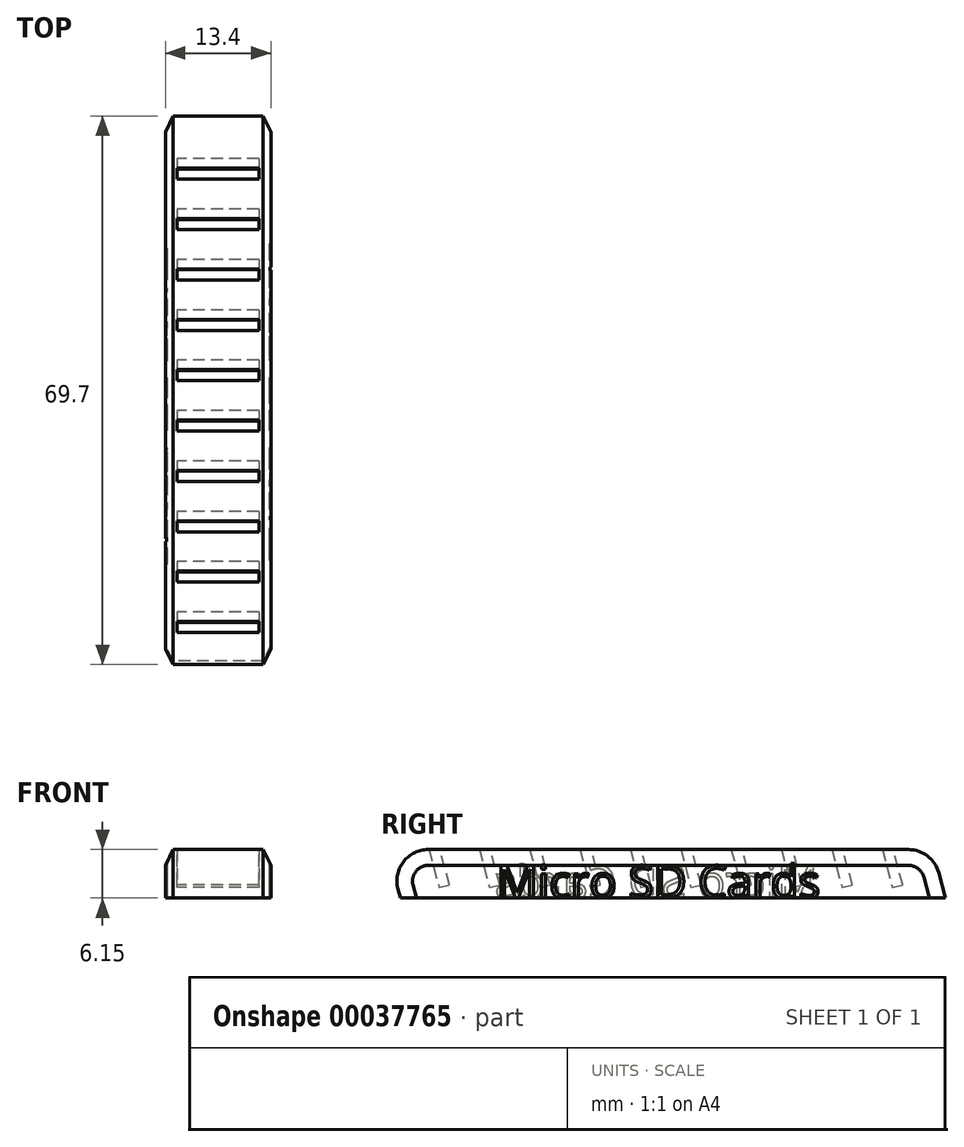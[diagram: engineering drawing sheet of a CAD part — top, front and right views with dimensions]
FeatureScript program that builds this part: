
annotation { "Feature Type Name" : "Feature", "Feature Type Description" : "" }
export const myFeature = defineFeature(function(context is Context, id is Id, definition is map)
    precondition{}
    {
        {
            assignVariable(context, id + "F0", {"name" : "tolerance", "anyValue" : 0.6});
        }
        {
            var Q0;
            Q0=qCreatedBy(makeId("Right.planeOp"),FACE);
            var sketch = newSketch(context, id + "F1", { "sketchPlane" : qUnion([Q0])});
            skLineSegment(sketch, "E0.bottom", {"start": v(-7.62, 0) * mm, "end": v(61.65, 0) * mm});
            skLineSegment(sketch, "E0.top", {"start": v(-9.26, 6.15) * mm, "end": v(60, 6.15) * mm, "construction": true});
            skLineSegment(sketch, "E1", {"start": v(-3.97, 6.15) * mm, "end": v(-2.68, 1.32) * mm});
            skLineSegment(sketch, "E2", {"start": v(-2.68, 1.32) * mm, "end": v(-1.37, 1.67) * mm});
            skLineSegment(sketch, "E3", {"start": v(-1.37, 1.67) * mm, "end": v(-2.57, 6.15) * mm});
            skLineSegment(sketch, "E4", {"start": v(-2.57, 6.15) * mm, "end": v(2.43, 6.15) * mm});
            skLineSegment(sketch, "E5.1.0.0", {"start": v(2.43, 6.15) * mm, "end": v(3.72, 1.32) * mm});
            skLineSegment(sketch, "E5.1.0.1", {"start": v(3.72, 1.32) * mm, "end": v(5.03, 1.67) * mm});
            skLineSegment(sketch, "E5.1.0.2", {"start": v(5.03, 1.67) * mm, "end": v(3.82, 6.15) * mm});
            skLineSegment(sketch, "E5.1.0.3", {"start": v(3.82, 6.15) * mm, "end": v(8.82, 6.15) * mm});
            skLineSegment(sketch, "E5.direction1", {"start": v(-2.68, 1.32) * mm, "end": v(3.72, 1.32) * mm, "construction": true});
            skLineSegment(sketch, "E6", {"start": v(-9.26, 6.15) * mm, "end": v(-3.97, 6.15) * mm});
            skLineSegment(sketch, "E7.0.2.0", {"start": v(8.82, 6.15) * mm, "end": v(10.12, 1.32) * mm});
            skLineSegment(sketch, "E7.3.2.0", {"start": v(10.12, 1.32) * mm, "end": v(11.42, 1.67) * mm});
            skLineSegment(sketch, "E7.6.2.0", {"start": v(11.42, 1.67) * mm, "end": v(10.22, 6.15) * mm});
            skLineSegment(sketch, "E7.9.2.0", {"start": v(10.22, 6.15) * mm, "end": v(15.22, 6.15) * mm});
            skLineSegment(sketch, "E8.0.3.0", {"start": v(15.22, 6.15) * mm, "end": v(16.52, 1.32) * mm});
            skLineSegment(sketch, "E8.3.3.0", {"start": v(16.52, 1.32) * mm, "end": v(17.82, 1.67) * mm});
            skLineSegment(sketch, "E8.6.3.0", {"start": v(17.82, 1.67) * mm, "end": v(16.62, 6.15) * mm});
            skLineSegment(sketch, "E8.9.3.0", {"start": v(16.62, 6.15) * mm, "end": v(21.62, 6.15) * mm});
            skLineSegment(sketch, "E9", {"start": v(60, 6.15) * mm, "end": v(61.65, 0) * mm});
            skLineSegment(sketch, "E10", {"start": v(-9.26, 6.15) * mm, "end": v(-7.62, 0) * mm});
            skLineSegment(sketch, "E11.0.4.0", {"start": v(21.62, 6.15) * mm, "end": v(22.91, 1.32) * mm});
            skLineSegment(sketch, "E11.3.4.0", {"start": v(22.91, 1.32) * mm, "end": v(24.22, 1.67) * mm});
            skLineSegment(sketch, "E11.6.4.0", {"start": v(24.22, 1.67) * mm, "end": v(23.02, 6.15) * mm});
            skLineSegment(sketch, "E11.9.4.0", {"start": v(23.02, 6.15) * mm, "end": v(28.02, 6.15) * mm});
            skLineSegment(sketch, "E11.0.5.0", {"start": v(28.02, 6.15) * mm, "end": v(29.31, 1.32) * mm});
            skLineSegment(sketch, "E11.3.5.0", {"start": v(29.31, 1.32) * mm, "end": v(30.62, 1.67) * mm});
            skLineSegment(sketch, "E11.6.5.0", {"start": v(30.62, 1.67) * mm, "end": v(29.42, 6.15) * mm});
            skLineSegment(sketch, "E11.9.5.0", {"start": v(29.42, 6.15) * mm, "end": v(34.42, 6.15) * mm});
            skLineSegment(sketch, "E11.0.6.0", {"start": v(34.42, 6.15) * mm, "end": v(35.7, 1.32) * mm});
            skLineSegment(sketch, "E11.3.6.0", {"start": v(35.7, 1.32) * mm, "end": v(37.01, 1.67) * mm});
            skLineSegment(sketch, "E11.6.6.0", {"start": v(37.01, 1.67) * mm, "end": v(35.81, 6.15) * mm});
            skLineSegment(sketch, "E11.9.6.0", {"start": v(35.81, 6.15) * mm, "end": v(40.81, 6.15) * mm});
            skLineSegment(sketch, "E11.0.7.0", {"start": v(40.81, 6.15) * mm, "end": v(42.1, 1.32) * mm});
            skLineSegment(sketch, "E11.3.7.0", {"start": v(42.1, 1.32) * mm, "end": v(43.41, 1.67) * mm});
            skLineSegment(sketch, "E11.6.7.0", {"start": v(43.41, 1.67) * mm, "end": v(42.21, 6.15) * mm});
            skLineSegment(sketch, "E11.9.7.0", {"start": v(42.21, 6.15) * mm, "end": v(47.21, 6.15) * mm});
            skLineSegment(sketch, "E11.0.8.0", {"start": v(47.21, 6.15) * mm, "end": v(48.5, 1.32) * mm});
            skLineSegment(sketch, "E11.3.8.0", {"start": v(48.5, 1.32) * mm, "end": v(49.8, 1.67) * mm});
            skLineSegment(sketch, "E11.6.8.0", {"start": v(49.8, 1.67) * mm, "end": v(48.6, 6.15) * mm});
            skLineSegment(sketch, "E11.9.8.0", {"start": v(48.6, 6.15) * mm, "end": v(53.6, 6.15) * mm});
            skLineSegment(sketch, "E11.0.9.0", {"start": v(53.6, 6.15) * mm, "end": v(54.9, 1.32) * mm});
            skLineSegment(sketch, "E11.3.9.0", {"start": v(54.9, 1.32) * mm, "end": v(56.2, 1.67) * mm});
            skLineSegment(sketch, "E11.6.9.0", {"start": v(56.2, 1.67) * mm, "end": v(55, 6.15) * mm});
            skLineSegment(sketch, "E11.9.9.0", {"start": v(55, 6.15) * mm, "end": v(60, 6.15) * mm});
            skSolve(sketch);
        }
        {
            var Q0;
            Q0=makeQuery(id+"F1.imprint","IMPRINT",FACE,{"disambiguationData":[TD([[makeQuery(id+"F1.imprint","IMPRINT",EDGE,{"derivedFrom":sQuery(id+"F1.wireOp",EDGE,"E0.bottom")}),1.0]])]});
            extrude(context, id + "F2", {"entities" : qUnion([Q0]), "depth" : (9.8 + getVariable(context, 'tolerance')) / 2 * mm});
        }
        {
            var Q0;
            Q0=makeQuery(id+"F2.opExtrude","CAP_FACE",FACE,{"disambiguationData":[OSD([sQuery(id+"F1.wireOp",EDGE,"E0.bottom"),sQuery(id+"F1.wireOp",EDGE,"E1"),sQuery(id+"F1.wireOp",EDGE,"E2"),sQuery(id+"F1.wireOp",EDGE,"E3"),sQuery(id+"F1.wireOp",EDGE,"E4"),sQuery(id+"F1.wireOp",EDGE,"E5.1.0.0"),sQuery(id+"F1.wireOp",EDGE,"E5.1.0.1"),sQuery(id+"F1.wireOp",EDGE,"E5.1.0.2"),sQuery(id+"F1.wireOp",EDGE,"E5.1.0.3"),sQuery(id+"F1.wireOp",EDGE,"E6"),sQuery(id+"F1.wireOp",EDGE,"E7.0.2.0"),sQuery(id+"F1.wireOp",EDGE,"E7.3.2.0"),sQuery(id+"F1.wireOp",EDGE,"E7.6.2.0"),sQuery(id+"F1.wireOp",EDGE,"E7.9.2.0"),sQuery(id+"F1.wireOp",EDGE,"E8.0.3.0"),sQuery(id+"F1.wireOp",EDGE,"E8.3.3.0"),sQuery(id+"F1.wireOp",EDGE,"E8.6.3.0"),sQuery(id+"F1.wireOp",EDGE,"E8.9.3.0"),sQuery(id+"F1.wireOp",EDGE,"E9"),sQuery(id+"F1.wireOp",EDGE,"E10"),sQuery(id+"F1.wireOp",EDGE,"E11.0.4.0"),sQuery(id+"F1.wireOp",EDGE,"E11.3.4.0"),sQuery(id+"F1.wireOp",EDGE,"E11.6.4.0"),sQuery(id+"F1.wireOp",EDGE,"E11.9.4.0"),sQuery(id+"F1.wireOp",EDGE,"E11.0.5.0"),sQuery(id+"F1.wireOp",EDGE,"E11.3.5.0"),sQuery(id+"F1.wireOp",EDGE,"E11.6.5.0"),sQuery(id+"F1.wireOp",EDGE,"E11.9.5.0"),sQuery(id+"F1.wireOp",EDGE,"E11.0.6.0"),sQuery(id+"F1.wireOp",EDGE,"E11.3.6.0"),sQuery(id+"F1.wireOp",EDGE,"E11.6.6.0"),sQuery(id+"F1.wireOp",EDGE,"E11.9.6.0"),sQuery(id+"F1.wireOp",EDGE,"E11.0.7.0"),sQuery(id+"F1.wireOp",EDGE,"E11.3.7.0"),sQuery(id+"F1.wireOp",EDGE,"E11.6.7.0"),sQuery(id+"F1.wireOp",EDGE,"E11.9.7.0"),sQuery(id+"F1.wireOp",EDGE,"E11.0.8.0"),sQuery(id+"F1.wireOp",EDGE,"E11.3.8.0"),sQuery(id+"F1.wireOp",EDGE,"E11.6.8.0"),sQuery(id+"F1.wireOp",EDGE,"E11.9.8.0"),sQuery(id+"F1.wireOp",EDGE,"E11.0.9.0"),sQuery(id+"F1.wireOp",EDGE,"E11.3.9.0"),sQuery(id+"F1.wireOp",EDGE,"E11.6.9.0"),sQuery(id+"F1.wireOp",EDGE,"E11.9.9.0")])],"isStart":false});
            var sketch = newSketch(context, id + "F3", { "sketchPlane" : qUnion([Q0])});
            skLineSegment(sketch, "E12", {"start": v(-9.26, 6.15) * mm, "end": v(-7.62, 0) * mm});
            skLineSegment(sketch, "E13", {"start": v(-7.62, 0) * mm, "end": v(61.65, 0) * mm});
            skLineSegment(sketch, "E14", {"start": v(61.65, 0) * mm, "end": v(60, 6.15) * mm});
            skLineSegment(sketch, "E15", {"start": v(60, 6.15) * mm, "end": v(-9.26, 6.15) * mm});
            skSolve(sketch);
        }
        {
            var Q0;
            {var subQ18=sQuery(id+"F3.wireOp",EDGE,"E12");Q0=makeQuery(id+"F3.imprint","IMPRINT",FACE,{"disambiguationData":[TD([[makeQuery(id+"F3.imprint","IMPRINT",EDGE,{"derivedFrom":subQ18}),1.0]])]});}
            var Q1;
            {var subQ1=makeQuery(id+"F2.opExtrude","CAP_EDGE",EDGE,{"disambiguationData":[OSD([sQuery(id+"F1.wireOp",EDGE,"E1")])],"isStart":false});Q1=makeQuery(id+"F3.imprint","IMPRINT",FACE,{"disambiguationData":[TD([[makeQuery(id+"F3.imprint","IMPRINT",EDGE,{"derivedFrom":subQ1}),1.0]])]});}
            var Q2;
            {var subQ1=makeQuery(id+"F2.opExtrude","CAP_EDGE",EDGE,{"disambiguationData":[OSD([sQuery(id+"F1.wireOp",EDGE,"E5.1.0.0")])],"isStart":false});Q2=makeQuery(id+"F3.imprint","IMPRINT",FACE,{"disambiguationData":[TD([[makeQuery(id+"F3.imprint","IMPRINT",EDGE,{"derivedFrom":subQ1}),1.0]])]});}
            var Q3;
            {var subQ1=makeQuery(id+"F2.opExtrude","CAP_EDGE",EDGE,{"disambiguationData":[OSD([sQuery(id+"F1.wireOp",EDGE,"E7.0.2.0")])],"isStart":false});Q3=makeQuery(id+"F3.imprint","IMPRINT",FACE,{"disambiguationData":[TD([[makeQuery(id+"F3.imprint","IMPRINT",EDGE,{"derivedFrom":subQ1}),1.0]])]});}
            var Q4;
            {var subQ0=makeQuery(id+"F2.opExtrude","CAP_EDGE",EDGE,{"disambiguationData":[OSD([sQuery(id+"F1.wireOp",EDGE,"E8.0.3.0")])],"isStart":false});Q4=makeQuery(id+"F3.imprint","IMPRINT",FACE,{"disambiguationData":[TD([[makeQuery(id+"F3.imprint","IMPRINT",EDGE,{"derivedFrom":subQ0}),1.0]])]});}
            var Q5;
            {var subQ1=makeQuery(id+"F2.opExtrude","CAP_EDGE",EDGE,{"disambiguationData":[OSD([sQuery(id+"F1.wireOp",EDGE,"E11.0.4.0")])],"isStart":false});Q5=makeQuery(id+"F3.imprint","IMPRINT",FACE,{"disambiguationData":[TD([[makeQuery(id+"F3.imprint","IMPRINT",EDGE,{"derivedFrom":subQ1}),1.0]])]});}
            var Q6;
            {var subQ1=makeQuery(id+"F2.opExtrude","CAP_EDGE",EDGE,{"disambiguationData":[OSD([sQuery(id+"F1.wireOp",EDGE,"E11.0.5.0")])],"isStart":false});Q6=makeQuery(id+"F3.imprint","IMPRINT",FACE,{"disambiguationData":[TD([[makeQuery(id+"F3.imprint","IMPRINT",EDGE,{"derivedFrom":subQ1}),1.0]])]});}
            var Q7;
            {var subQ1=makeQuery(id+"F2.opExtrude","CAP_EDGE",EDGE,{"disambiguationData":[OSD([sQuery(id+"F1.wireOp",EDGE,"E11.0.6.0")])],"isStart":false});Q7=makeQuery(id+"F3.imprint","IMPRINT",FACE,{"disambiguationData":[TD([[makeQuery(id+"F3.imprint","IMPRINT",EDGE,{"derivedFrom":subQ1}),1.0]])]});}
            var Q8;
            {var subQ1=makeQuery(id+"F2.opExtrude","CAP_EDGE",EDGE,{"disambiguationData":[OSD([sQuery(id+"F1.wireOp",EDGE,"E11.0.7.0")])],"isStart":false});Q8=makeQuery(id+"F3.imprint","IMPRINT",FACE,{"disambiguationData":[TD([[makeQuery(id+"F3.imprint","IMPRINT",EDGE,{"derivedFrom":subQ1}),1.0]])]});}
            var Q9;
            {var subQ0=makeQuery(id+"F2.opExtrude","CAP_EDGE",EDGE,{"disambiguationData":[OSD([sQuery(id+"F1.wireOp",EDGE,"E11.0.8.0")])],"isStart":false});Q9=makeQuery(id+"F3.imprint","IMPRINT",FACE,{"disambiguationData":[TD([[makeQuery(id+"F3.imprint","IMPRINT",EDGE,{"derivedFrom":subQ0}),1.0]])]});}
            var Q10;
            {var subQ1=makeQuery(id+"F2.opExtrude","CAP_EDGE",EDGE,{"disambiguationData":[OSD([sQuery(id+"F1.wireOp",EDGE,"E11.0.9.0")])],"isStart":false});Q10=makeQuery(id+"F3.imprint","IMPRINT",FACE,{"disambiguationData":[TD([[makeQuery(id+"F3.imprint","IMPRINT",EDGE,{"derivedFrom":subQ1}),1.0]])]});}
            extrude(context, id + "F4", {"entities" : qUnion([Q0, Q1, Q2, Q3, Q4, Q5, Q6, Q7, Q8, Q9, Q10]), "operationType" : NewBodyOperationType.ADD, "depth" : 1.5 * mm});
        }
        {
            var Q0;
            Q0=makeQuery(id+"F2.opExtrude","SWEPT_BODY",BODY,{"disambiguationData":[OSD([sQuery(id+"F1.wireOp",EDGE,"E0.bottom"),sQuery(id+"F1.wireOp",EDGE,"E1"),sQuery(id+"F1.wireOp",EDGE,"E2"),sQuery(id+"F1.wireOp",EDGE,"E3"),sQuery(id+"F1.wireOp",EDGE,"E4"),sQuery(id+"F1.wireOp",EDGE,"E5.1.0.0"),sQuery(id+"F1.wireOp",EDGE,"E5.1.0.1"),sQuery(id+"F1.wireOp",EDGE,"E5.1.0.2"),sQuery(id+"F1.wireOp",EDGE,"E5.1.0.3"),sQuery(id+"F1.wireOp",EDGE,"E6"),sQuery(id+"F1.wireOp",EDGE,"E7.0.2.0"),sQuery(id+"F1.wireOp",EDGE,"E7.3.2.0"),sQuery(id+"F1.wireOp",EDGE,"E7.6.2.0"),sQuery(id+"F1.wireOp",EDGE,"E7.9.2.0"),sQuery(id+"F1.wireOp",EDGE,"E8.0.3.0"),sQuery(id+"F1.wireOp",EDGE,"E8.3.3.0"),sQuery(id+"F1.wireOp",EDGE,"E8.6.3.0"),sQuery(id+"F1.wireOp",EDGE,"E8.9.3.0"),sQuery(id+"F1.wireOp",EDGE,"E9"),sQuery(id+"F1.wireOp",EDGE,"E10"),sQuery(id+"F1.wireOp",EDGE,"E11.0.4.0"),sQuery(id+"F1.wireOp",EDGE,"E11.3.4.0"),sQuery(id+"F1.wireOp",EDGE,"E11.6.4.0"),sQuery(id+"F1.wireOp",EDGE,"E11.9.4.0"),sQuery(id+"F1.wireOp",EDGE,"E11.0.5.0"),sQuery(id+"F1.wireOp",EDGE,"E11.3.5.0"),sQuery(id+"F1.wireOp",EDGE,"E11.6.5.0"),sQuery(id+"F1.wireOp",EDGE,"E11.9.5.0"),sQuery(id+"F1.wireOp",EDGE,"E11.0.6.0"),sQuery(id+"F1.wireOp",EDGE,"E11.3.6.0"),sQuery(id+"F1.wireOp",EDGE,"E11.6.6.0"),sQuery(id+"F1.wireOp",EDGE,"E11.9.6.0"),sQuery(id+"F1.wireOp",EDGE,"E11.0.7.0"),sQuery(id+"F1.wireOp",EDGE,"E11.3.7.0"),sQuery(id+"F1.wireOp",EDGE,"E11.6.7.0"),sQuery(id+"F1.wireOp",EDGE,"E11.9.7.0"),sQuery(id+"F1.wireOp",EDGE,"E11.0.8.0"),sQuery(id+"F1.wireOp",EDGE,"E11.3.8.0"),sQuery(id+"F1.wireOp",EDGE,"E11.6.8.0"),sQuery(id+"F1.wireOp",EDGE,"E11.9.8.0"),sQuery(id+"F1.wireOp",EDGE,"E11.0.9.0"),sQuery(id+"F1.wireOp",EDGE,"E11.3.9.0"),sQuery(id+"F1.wireOp",EDGE,"E11.6.9.0"),sQuery(id+"F1.wireOp",EDGE,"E11.9.9.0")])]});
            var Q1;
            Q1=makeQuery(id+"F2.opExtrude","CAP_FACE",FACE,{"disambiguationData":[OSD([sQuery(id+"F1.wireOp",EDGE,"E0.bottom"),sQuery(id+"F1.wireOp",EDGE,"E1"),sQuery(id+"F1.wireOp",EDGE,"E2"),sQuery(id+"F1.wireOp",EDGE,"E3"),sQuery(id+"F1.wireOp",EDGE,"E4"),sQuery(id+"F1.wireOp",EDGE,"E5.1.0.0"),sQuery(id+"F1.wireOp",EDGE,"E5.1.0.1"),sQuery(id+"F1.wireOp",EDGE,"E5.1.0.2"),sQuery(id+"F1.wireOp",EDGE,"E5.1.0.3"),sQuery(id+"F1.wireOp",EDGE,"E6"),sQuery(id+"F1.wireOp",EDGE,"E7.0.2.0"),sQuery(id+"F1.wireOp",EDGE,"E7.3.2.0"),sQuery(id+"F1.wireOp",EDGE,"E7.6.2.0"),sQuery(id+"F1.wireOp",EDGE,"E7.9.2.0"),sQuery(id+"F1.wireOp",EDGE,"E8.0.3.0"),sQuery(id+"F1.wireOp",EDGE,"E8.3.3.0"),sQuery(id+"F1.wireOp",EDGE,"E8.6.3.0"),sQuery(id+"F1.wireOp",EDGE,"E8.9.3.0"),sQuery(id+"F1.wireOp",EDGE,"E9"),sQuery(id+"F1.wireOp",EDGE,"E10"),sQuery(id+"F1.wireOp",EDGE,"E11.0.4.0"),sQuery(id+"F1.wireOp",EDGE,"E11.3.4.0"),sQuery(id+"F1.wireOp",EDGE,"E11.6.4.0"),sQuery(id+"F1.wireOp",EDGE,"E11.9.4.0"),sQuery(id+"F1.wireOp",EDGE,"E11.0.5.0"),sQuery(id+"F1.wireOp",EDGE,"E11.3.5.0"),sQuery(id+"F1.wireOp",EDGE,"E11.6.5.0"),sQuery(id+"F1.wireOp",EDGE,"E11.9.5.0"),sQuery(id+"F1.wireOp",EDGE,"E11.0.6.0"),sQuery(id+"F1.wireOp",EDGE,"E11.3.6.0"),sQuery(id+"F1.wireOp",EDGE,"E11.6.6.0"),sQuery(id+"F1.wireOp",EDGE,"E11.9.6.0"),sQuery(id+"F1.wireOp",EDGE,"E11.0.7.0"),sQuery(id+"F1.wireOp",EDGE,"E11.3.7.0"),sQuery(id+"F1.wireOp",EDGE,"E11.6.7.0"),sQuery(id+"F1.wireOp",EDGE,"E11.9.7.0"),sQuery(id+"F1.wireOp",EDGE,"E11.0.8.0"),sQuery(id+"F1.wireOp",EDGE,"E11.3.8.0"),sQuery(id+"F1.wireOp",EDGE,"E11.6.8.0"),sQuery(id+"F1.wireOp",EDGE,"E11.9.8.0"),sQuery(id+"F1.wireOp",EDGE,"E11.0.9.0"),sQuery(id+"F1.wireOp",EDGE,"E11.3.9.0"),sQuery(id+"F1.wireOp",EDGE,"E11.6.9.0"),sQuery(id+"F1.wireOp",EDGE,"E11.9.9.0")])],"isStart":true});
            mirror(context, id + "F5", {"operationType" : NewBodyOperationType.ADD, "entities" : qUnion([Q0]), "mirrorPlane" : qUnion([Q1])});
        }
        {
            var Q0;
            {var subQ0=makeQuery(id+"F4.boolean.opBoolean","MERGE",EDGE,{"derivedFrom":[makeQuery(id+"F2.opExtrude","SWEPT_EDGE",EDGE,{"disambiguationData":[OSD([sQuery(id+"F1.wireOp",EDGE,"E9"),sQuery(id+"F1.wireOp",EDGE,"E11.9.9.0")])]}),makeQuery(id+"F4.opExtrude","SWEPT_EDGE",EDGE,{"disambiguationData":[OSD([sQuery(id+"F3.wireOp",EDGE,"E14"),sQuery(id+"F3.wireOp",EDGE,"E15")])]})]});Q0=makeQuery(id+"F5.boolean.opBoolean","MERGE",EDGE,{"derivedFrom":[subQ0,makeQuery(id+"F5.opPattern","COPY",EDGE,{"derivedFrom":subQ0,"instanceName":"1"})]});}
            var Q1;
            {var subQ0=makeQuery(id+"F4.boolean.opBoolean","MERGE",EDGE,{"derivedFrom":[makeQuery(id+"F2.opExtrude","SWEPT_EDGE",EDGE,{"disambiguationData":[OSD([sQuery(id+"F1.wireOp",EDGE,"E6"),sQuery(id+"F1.wireOp",EDGE,"E10")])]}),makeQuery(id+"F4.opExtrude","SWEPT_EDGE",EDGE,{"disambiguationData":[OSD([sQuery(id+"F3.wireOp",EDGE,"E12"),sQuery(id+"F3.wireOp",EDGE,"E15")])]})]});Q1=makeQuery(id+"F5.boolean.opBoolean","MERGE",EDGE,{"derivedFrom":[subQ0,makeQuery(id+"F5.opPattern","COPY",EDGE,{"derivedFrom":subQ0,"instanceName":"1"})]});}
            fillet(context, id + "F6", {"entities" : qUnion([Q0, Q1]), "radius" : 4 * mm, "tangentPropagation" : true, "allowEdgeOverflow" : false});
        }
        {
            var Q0;
            Q0=makeQuery(id+"F5.opPattern","COPY",EDGE,{"derivedFrom":makeQuery(id+"F4.opExtrude","CAP_EDGE",EDGE,{"disambiguationData":[OSD([sQuery(id+"F3.wireOp",EDGE,"E15")])],"isStart":false}),"instanceName":"1"});
            var Q1;
            Q1=makeQuery(id+"F4.opExtrude","CAP_EDGE",EDGE,{"disambiguationData":[OSD([sQuery(id+"F3.wireOp",EDGE,"E15")])],"isStart":false});
            chamfer(context, id + "F7", {"entities" : qUnion([Q0, Q1]), "chamferType" : ChamferType.TWO_OFFSETS, "width1" : 1 * mm, "oppositeDirection" : true, "width2" : 2 * mm, "tangentPropagation" : true});
        }
        {
            var Q0;
            Q0=makeQuery(id+"F4.opExtrude","CAP_FACE",FACE,{"disambiguationData":[OSD([sQuery(id+"F3.wireOp",EDGE,"E12"),sQuery(id+"F3.wireOp",EDGE,"E13"),sQuery(id+"F3.wireOp",EDGE,"E14"),sQuery(id+"F3.wireOp",EDGE,"E15")])],"isStart":false});
            var sketch = newSketch(context, id + "F8", { "sketchPlane" : qUnion([Q0])});
            skText(sketch, "E16", { "text": "Micro SD Cards", "fontName": "OpenSans-Regular.ttf"});
            skLineSegment(sketch, "E17", {"start": v(6.04, 4.15) * mm, "end": v(-4.05, 4.15) * mm, "construction": true});
            skLineSegment(sketch, "E18", {"start": v(46.85, 4.15) * mm, "end": v(56.94, 4.15) * mm, "construction": true});
            const initialGuessF8  = {"E16": [0.00464, 0, 1, 0, 0.00415]};
            skSetInitialGuess(sketch, initialGuessF8);
            skSolve(sketch);
        }
        {
            var Q0;
            Q0 = qSketchRegion(id + "F8", true);
            extrude(context, id + "F9", {"entities" : qUnion([Q0]), "operationType" : NewBodyOperationType.REMOVE, "oppositeDirection" : true, "depth" : 0.2 * mm});
        }
        {
            var Q0;
            Q0=makeQuery(id+"F5.opPattern","COPY",FACE,{"derivedFrom":makeQuery(id+"F4.opExtrude","CAP_FACE",FACE,{"disambiguationData":[OSD([sQuery(id+"F3.wireOp",EDGE,"E12"),sQuery(id+"F3.wireOp",EDGE,"E13"),sQuery(id+"F3.wireOp",EDGE,"E14"),sQuery(id+"F3.wireOp",EDGE,"E15")])],"isStart":false}),"instanceName":"1"});
            var sketch = newSketch(context, id + "F10", { "sketchPlane" : qUnion([Q0])});
            skText(sketch, "E19", { "text": "Micro SD Cards", "fontName": "OpenSans-Regular.ttf"});
            skLineSegment(sketch, "E20", {"start": v(-46.85, 4.15) * mm, "end": v(-56.94, 4.15) * mm, "construction": true});
            skLineSegment(sketch, "E21", {"start": v(-6.04, 4.15) * mm, "end": v(4.05, 4.15) * mm, "construction": true});
            const initialGuessF10  = {"E19": [-0.04545, 0, 1, 0, 0.00415]};
            skSetInitialGuess(sketch, initialGuessF10);
            skSolve(sketch);
        }
        {
            var Q0;
            Q0 = qSketchRegion(id + "F10", true);
            extrude(context, id + "F11", {"entities" : qUnion([Q0]), "operationType" : NewBodyOperationType.REMOVE, "oppositeDirection" : true, "depth" : 0.2 * mm});
        }
    });
